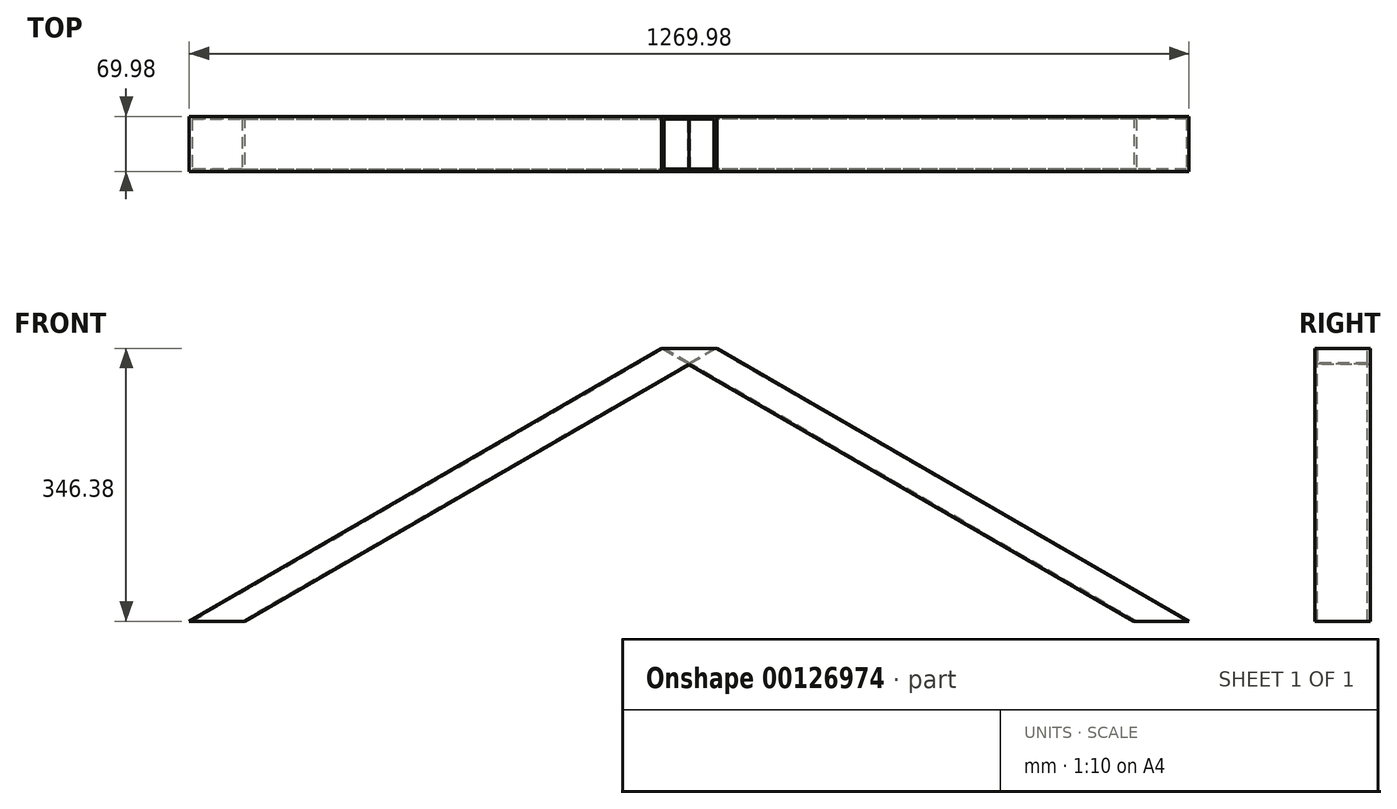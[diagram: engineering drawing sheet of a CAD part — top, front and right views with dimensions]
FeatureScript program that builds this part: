
annotation { "Feature Type Name" : "Feature", "Feature Type Description" : "" }
export const myFeature = defineFeature(function(context is Context, id is Id, definition is map)
    precondition{}
    {
        {
            var Q0;
            Q0=qCreatedBy(makeId("Front.planeOp"),FACE);
            var sketch = newSketch(context, id + "F0", { "sketchPlane" : qUnion([Q0])});
            skLineSegment(sketch, "E0", {"start": v(0, 0) * mm, "end": v(599.95, 346.38) * mm});
            skLineSegment(sketch, "E1", {"start": v(599.95, 346.38) * mm, "end": v(1199.9, 0) * mm});
            skSolve(sketch);
        }
        {
            var Q0;
            Q0=qCreatedBy(makeId("Top.planeOp"),FACE);
            var sketch = newSketch(context, id + "F1", { "sketchPlane" : qUnion([Q0])});
            skLineSegment(sketch, "E2.bottom", {"start": v(31.75, 31.75) * mm, "end": v(-31.75, 31.75) * mm});
            skLineSegment(sketch, "E2.top", {"start": v(31.75, -31.75) * mm, "end": v(-31.75, -31.75) * mm});
            skLineSegment(sketch, "E2.left", {"start": v(31.75, 31.75) * mm, "end": v(31.75, -31.75) * mm});
            skLineSegment(sketch, "E2.right", {"start": v(-31.75, 31.75) * mm, "end": v(-31.75, -31.75) * mm});
            skPoint(sketch, "E2.middle", {"position": v(0, 0) * mm});
            skLineSegment(sketch, "E3.bottom", {"start": v(34.99, 34.99) * mm, "end": v(-34.99, 34.99) * mm});
            skLineSegment(sketch, "E3.top", {"start": v(34.99, -34.99) * mm, "end": v(-34.99, -34.99) * mm});
            skLineSegment(sketch, "E3.left", {"start": v(34.99, 34.99) * mm, "end": v(34.99, -34.99) * mm});
            skLineSegment(sketch, "E3.right", {"start": v(-34.99, 34.99) * mm, "end": v(-34.99, -34.99) * mm});
            skLineSegment(sketch, "E4.bottom", {"start": v(1234.99, 34.99) * mm, "end": v(1165, 34.99) * mm});
            skLineSegment(sketch, "E4.top", {"start": v(1234.99, -34.99) * mm, "end": v(1165, -34.99) * mm});
            skLineSegment(sketch, "E4.left", {"start": v(1234.99, 34.99) * mm, "end": v(1234.99, -34.99) * mm});
            skLineSegment(sketch, "E4.right", {"start": v(1165, 34.99) * mm, "end": v(1165, -34.99) * mm});
            skPoint(sketch, "E4.middle", {"position": v(1200, 0) * mm});
            skLineSegment(sketch, "E5.bottom", {"start": v(1231.75, 31.75) * mm, "end": v(1168.25, 31.75) * mm});
            skLineSegment(sketch, "E5.top", {"start": v(1231.75, -31.75) * mm, "end": v(1168.25, -31.75) * mm});
            skLineSegment(sketch, "E5.left", {"start": v(1231.75, 31.75) * mm, "end": v(1231.75, -31.75) * mm});
            skLineSegment(sketch, "E5.right", {"start": v(1168.25, 31.75) * mm, "end": v(1168.25, -31.75) * mm});
            skSolve(sketch);
        }
        {
            var Q0;
            Q0=makeQuery(id+"F1.imprint","IMPRINT",FACE,{"disambiguationData":[TD([[makeQuery(id+"F1.imprint","IMPRINT",EDGE,{"derivedFrom":sQuery(id+"F1.wireOp",EDGE,"E4.bottom")}),1.0]])]});
            var Q1;
            Q1=sQuery(id+"F0.wireOp",EDGE,"E1");
            sweep(context, id + "F2", {"profiles" : qUnion([Q0]), "path" : qUnion([Q1])});
        }
        {
            var Q0;
            Q0=qCreatedBy(makeId("Front.planeOp"),FACE);
            var sketch = newSketch(context, id + "F3", { "sketchPlane" : qUnion([Q0])});
            skLineSegment(sketch, "E6", {"start": v(0, 0) * mm, "end": v(599.95, 346.38) * mm});
            skSolve(sketch);
        }
        {
            var Q0;
            Q0=qCreatedBy(makeId("Top.planeOp"),FACE);
            var sketch = newSketch(context, id + "F4", { "sketchPlane" : qUnion([Q0])});
            skLineSegment(sketch, "E7.bottom", {"start": v(34.99, 34.99) * mm, "end": v(-34.99, 34.99) * mm});
            skLineSegment(sketch, "E7.top", {"start": v(34.99, -34.99) * mm, "end": v(-34.99, -34.99) * mm});
            skLineSegment(sketch, "E7.left", {"start": v(34.99, 34.99) * mm, "end": v(34.99, -34.99) * mm});
            skLineSegment(sketch, "E7.right", {"start": v(-34.99, 34.99) * mm, "end": v(-34.99, -34.99) * mm});
            skPoint(sketch, "E7.middle", {"position": v(0, 0) * mm});
            skLineSegment(sketch, "E8.bottom", {"start": v(31.75, 31.75) * mm, "end": v(-31.75, 31.75) * mm});
            skLineSegment(sketch, "E8.top", {"start": v(31.75, -31.75) * mm, "end": v(-31.75, -31.75) * mm});
            skLineSegment(sketch, "E8.left", {"start": v(31.75, 31.75) * mm, "end": v(31.75, -31.75) * mm});
            skLineSegment(sketch, "E8.right", {"start": v(-31.75, 31.75) * mm, "end": v(-31.75, -31.75) * mm});
            skSolve(sketch);
        }
        {
            var Q0;
            Q0=makeQuery(id+"F4.imprint","IMPRINT",FACE,{"disambiguationData":[TD([[makeQuery(id+"F4.imprint","IMPRINT",EDGE,{"derivedFrom":sQuery(id+"F4.wireOp",EDGE,"E7.bottom")}),1.0]])]});
            var Q1;
            Q1=sQuery(id+"F3.wireOp",EDGE,"E6");
            sweep(context, id + "F5", {"operationType" : NewBodyOperationType.ADD, "profiles" : qUnion([Q0]), "path" : qUnion([Q1])});
        }
    });
